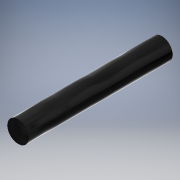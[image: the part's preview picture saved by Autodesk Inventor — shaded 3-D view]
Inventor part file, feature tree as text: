
AUTODESK INVENTOR PART (.ipt)
format: ipt  version: 2017 (Build 210142000, 142)  size: 90,624 bytes
history: native  units: mm
features: extrude x1, sketch x1
ambient origin geometry x8: Origin, YZ Plane, XZ Plane, XY Plane, X Axis, Y Axis, Z Axis, Center Point
bodies: Solid1 (feature_tree)
feature tree (2):
  extrude  "Extrusion1"  Depth=10.0mm TaperAngle=0.0deg
  sketch  "Sketch1"  dims[d0=1.5mm d1=10.0mm d2=0.0mm]
